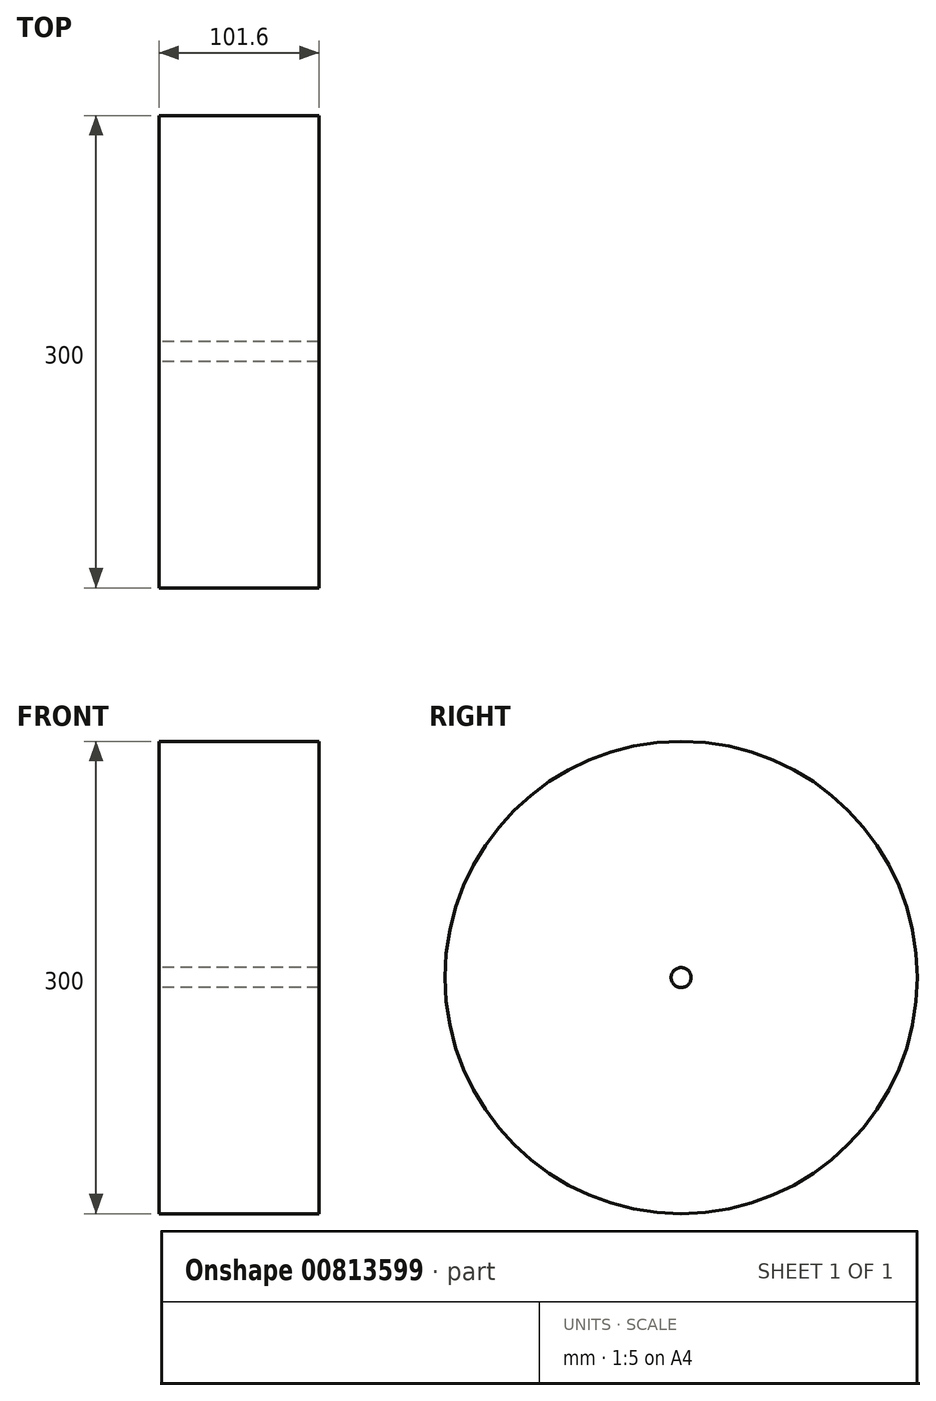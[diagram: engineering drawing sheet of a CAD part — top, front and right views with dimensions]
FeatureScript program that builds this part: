
annotation { "Feature Type Name" : "Feature", "Feature Type Description" : "" }
export const myFeature = defineFeature(function(context is Context, id is Id, definition is map)
    precondition{}
    {
        {
            var Q0;
            Q0=qCreatedBy(makeId("Right.planeOp"),FACE);
            var sketch = newSketch(context, id + "F0", { "sketchPlane" : qUnion([Q0])});
            skCircle(sketch, "E0", {"center": v(0, 0) * mm, "radius": 150 * mm});
            skCircle(sketch, "E1", {"center": v(0, 0) * mm, "radius": 6.35 * mm});
            skSolve(sketch);
        }
        {
            var Q0;
            Q0=makeQuery(id+"F0.imprint","IMPRINT",FACE,{"disambiguationData":[TD([[makeQuery(id+"F0.imprint","IMPRINT",EDGE,{"derivedFrom":sQuery(id+"F0.wireOp",EDGE,"E0")}),1.0]])]});
            extrude(context, id + "F1", {"entities" : qUnion([Q0]), "depth" : 101.6 * mm, "offsetDistance" : 25.4 * mm});
        }
    });
